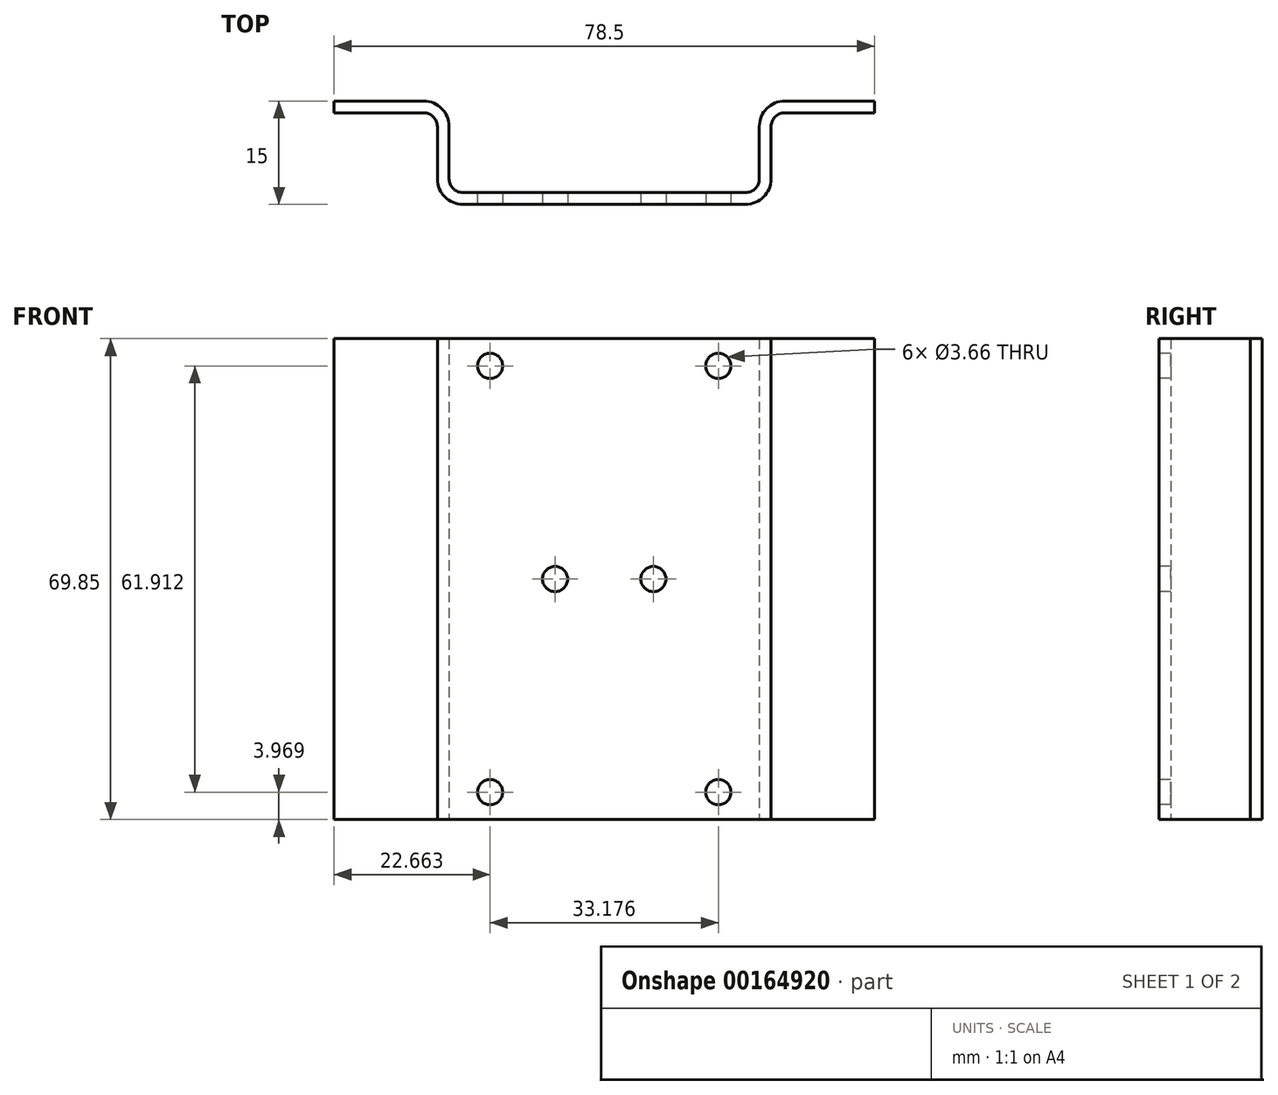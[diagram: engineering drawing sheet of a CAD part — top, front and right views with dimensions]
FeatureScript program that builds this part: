
annotation { "Feature Type Name" : "Feature", "Feature Type Description" : "" }
export const myFeature = defineFeature(function(context is Context, id is Id, definition is map)
    precondition{}
    {
        {
            var Q0;
            Q0=qCreatedBy(makeId("Top.planeOp"),FACE);
            var sketch = newSketch(context, id + "F0", { "sketchPlane" : qUnion([Q0])});
            skLineSegment(sketch, "E0", {"start": v(0, 0) * mm, "end": v(0, -13.3) * mm});
            skLineSegment(sketch, "E1", {"start": v(0, -13.3) * mm, "end": v(45.08, -13.3) * mm});
            skLineSegment(sketch, "E2", {"start": v(46.8, -15) * mm, "end": v(-1.7, -15) * mm});
            skLineSegment(sketch, "E3", {"start": v(-1.7, -15) * mm, "end": v(-1.7, -1.7) * mm});
            skLineSegment(sketch, "E4", {"start": v(0, -13.3) * mm, "end": v(-1.7, -13.3) * mm, "construction": true});
            skLineSegment(sketch, "E5", {"start": v(22.54, -15) * mm, "end": v(22.54, -13.3) * mm, "construction": true});
            skLineSegment(sketch, "E6", {"start": v(45.08, -13.3) * mm, "end": v(45.08, 0) * mm});
            skLineSegment(sketch, "E7", {"start": v(46.8, -1.7) * mm, "end": v(46.8, -15) * mm});
            skLineSegment(sketch, "E8", {"start": v(0, 0) * mm, "end": v(-16.7, 0) * mm});
            skLineSegment(sketch, "E9", {"start": v(-16.7, 0) * mm, "end": v(-16.7, -1.7) * mm});
            skLineSegment(sketch, "E10", {"start": v(-16.7, -1.7) * mm, "end": v(-1.7, -1.7) * mm});
            skLineSegment(sketch, "E11", {"start": v(46.8, -1.7) * mm, "end": v(61.8, -1.7) * mm});
            skLineSegment(sketch, "E12", {"start": v(61.8, -1.7) * mm, "end": v(61.8, 0) * mm});
            skLineSegment(sketch, "E13", {"start": v(61.8, 0) * mm, "end": v(45.08, 0) * mm});
            skPoint(sketch, "E14", {"position": v(-9.2, -1.7) * mm});
            skPoint(sketch, "E15", {"position": v(54.3, -1.7) * mm});
            skSolve(sketch);
        }
        {
            var Q0;
            Q0=qSketchRegion(id+"F0",true);
            extrude(context, id + "F1", {"entities" : qUnion([Q0]), "depth" : 69.85 * mm});
        }
        {
            var Q0;
            Q0=makeQuery(id+"F1.opExtrude","SWEPT_EDGE",EDGE,{"disambiguationData":[OSD([sQuery(id+"F0.wireOp",EDGE,"E2"),sQuery(id+"F0.wireOp",EDGE,"E7")])]});
            var Q1;
            Q1=makeQuery(id+"F1.opExtrude","SWEPT_EDGE",EDGE,{"disambiguationData":[OSD([sQuery(id+"F0.wireOp",EDGE,"E2"),sQuery(id+"F0.wireOp",EDGE,"E7")])]});
            var Q2;
            Q2=makeQuery(id+"F1.opExtrude","SWEPT_EDGE",EDGE,{"disambiguationData":[OSD([sQuery(id+"F0.wireOp",EDGE,"E2"),sQuery(id+"F0.wireOp",EDGE,"E3")])]});
            var Q3;
            Q3=makeQuery(id+"F1.opExtrude","SWEPT_EDGE",EDGE,{"disambiguationData":[OSD([sQuery(id+"F0.wireOp",EDGE,"E2"),sQuery(id+"F0.wireOp",EDGE,"E3")])]});
            var Q4;
            Q4=makeQuery(id+"F1.opExtrude","SWEPT_EDGE",EDGE,{"disambiguationData":[OSD([sQuery(id+"F0.wireOp",EDGE,"E0"),sQuery(id+"F0.wireOp",EDGE,"E8")])]});
            var Q5;
            Q5=makeQuery(id+"F1.opExtrude","SWEPT_EDGE",EDGE,{"disambiguationData":[OSD([sQuery(id+"F0.wireOp",EDGE,"E6"),sQuery(id+"F0.wireOp",EDGE,"E13")])]});
            fillet(context, id + "F2", {"entities" : qUnion([Q0, Q1, Q2, Q3, Q4, Q5]), "radius" : 3.7 * mm, "tangentPropagation" : true, "allowEdgeOverflow" : false});
        }
        {
            var Q0;
            Q0=makeQuery(id+"F1.opExtrude","SWEPT_EDGE",EDGE,{"disambiguationData":[OSD([sQuery(id+"F0.wireOp",EDGE,"E0"),sQuery(id+"F0.wireOp",EDGE,"E1")])]});
            var Q1;
            Q1=makeQuery(id+"F1.opExtrude","SWEPT_EDGE",EDGE,{"disambiguationData":[OSD([sQuery(id+"F0.wireOp",EDGE,"E1"),sQuery(id+"F0.wireOp",EDGE,"E6")])]});
            var Q2;
            Q2=makeQuery(id+"F1.opExtrude","SWEPT_EDGE",EDGE,{"disambiguationData":[OSD([sQuery(id+"F0.wireOp",EDGE,"E1"),sQuery(id+"F0.wireOp",EDGE,"E6")])]});
            var Q3;
            Q3=makeQuery(id+"F1.opExtrude","SWEPT_EDGE",EDGE,{"disambiguationData":[OSD([sQuery(id+"F0.wireOp",EDGE,"E0"),sQuery(id+"F0.wireOp",EDGE,"E1")])]});
            var Q4;
            Q4=makeQuery(id+"F1.opExtrude","SWEPT_EDGE",EDGE,{"disambiguationData":[OSD([sQuery(id+"F0.wireOp",EDGE,"E7"),sQuery(id+"F0.wireOp",EDGE,"E11")])]});
            var Q5;
            Q5=makeQuery(id+"F1.opExtrude","SWEPT_EDGE",EDGE,{"disambiguationData":[OSD([sQuery(id+"F0.wireOp",EDGE,"E3"),sQuery(id+"F0.wireOp",EDGE,"E10")])]});
            fillet(context, id + "F3", {"entities" : qUnion([Q0, Q1, Q2, Q3, Q4, Q5]), "radius" : 1.98 * mm, "tangentPropagation" : true, "allowEdgeOverflow" : false});
        }
        {
            var Q0;
            Q0=makeQuery(id+"F1.opExtrude","SWEPT_FACE",FACE,{"disambiguationData":[OSD([sQuery(id+"F0.wireOp",EDGE,"E2")])]});
            var sketch = newSketch(context, id + "F4", { "sketchPlane" : qUnion([Q0])});
            skLineSegment(sketch, "E16", {"start": v(43.1, 34.93) * mm, "end": v(39.13, 34.93) * mm, "construction": true});
            skLineSegment(sketch, "E17.bottom", {"start": v(39.13, 65.88) * mm, "end": v(5.95, 65.88) * mm, "construction": true});
            skLineSegment(sketch, "E17.top", {"start": v(39.13, 3.97) * mm, "end": v(5.95, 3.97) * mm, "construction": true});
            skLineSegment(sketch, "E17.left", {"start": v(39.13, 65.88) * mm, "end": v(39.13, 3.97) * mm, "construction": true});
            skLineSegment(sketch, "E17.right", {"start": v(5.95, 65.88) * mm, "end": v(5.95, 3.97) * mm, "construction": true});
            skCircle(sketch, "E18", {"center": v(39.13, 65.88) * mm, "radius": 1.83 * mm});
            skCircle(sketch, "E19", {"center": v(5.95, 65.88) * mm, "radius": 1.83 * mm});
            skCircle(sketch, "E20", {"center": v(5.95, 3.97) * mm, "radius": 1.83 * mm});
            skCircle(sketch, "E21", {"center": v(39.13, 3.97) * mm, "radius": 1.83 * mm});
            skLineSegment(sketch, "E22", {"start": v(5.95, 34.93) * mm, "end": v(1.98, 34.93) * mm, "construction": true});
            skLineSegment(sketch, "E23", {"start": v(22.54, 3.97) * mm, "end": v(22.54, 0) * mm, "construction": true});
            skLineSegment(sketch, "E24", {"start": v(5.95, 34.93) * mm, "end": v(15.4, 34.93) * mm, "construction": true});
            skLineSegment(sketch, "E25", {"start": v(15.4, 34.93) * mm, "end": v(29.68, 34.93) * mm, "construction": true});
            skLineSegment(sketch, "E26", {"start": v(29.68, 34.93) * mm, "end": v(39.13, 34.93) * mm, "construction": true});
            skCircle(sketch, "E27", {"center": v(15.4, 34.93) * mm, "radius": 1.83 * mm});
            skCircle(sketch, "E28", {"center": v(29.68, 34.93) * mm, "radius": 1.83 * mm});
            skSolve(sketch);
        }
        {
            var Q0;
            Q0=qSketchRegion(id+"F4",true);
            var Q1;
            Q1=makeQuery(id+"F1.opExtrude","SWEPT_FACE",FACE,{"disambiguationData":[OSD([sQuery(id+"F0.wireOp",EDGE,"E1")])]});
            extrude(context, id + "F5", {"entities" : qUnion([Q0]), "operationType" : NewBodyOperationType.REMOVE, "endBound" : BoundingType.UP_TO_SURFACE, "oppositeDirection" : true, "endBoundEntityFace" : qUnion([Q1]), "depth" : 25.4 * mm});
        }
    });
